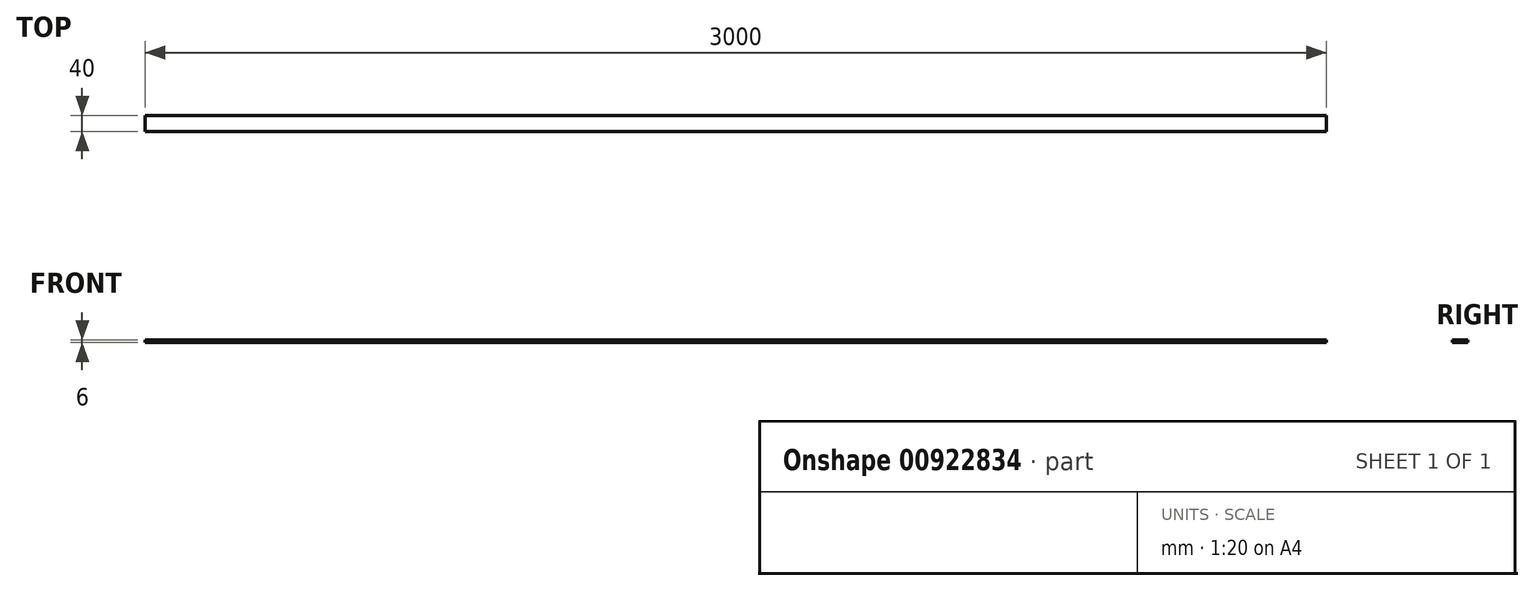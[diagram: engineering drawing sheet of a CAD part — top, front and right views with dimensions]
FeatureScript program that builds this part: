
annotation { "Feature Type Name" : "Feature", "Feature Type Description" : "" }
export const myFeature = defineFeature(function(context is Context, id is Id, definition is map)
    precondition{}
    {
        {
            var Q0;
            Q0=qCreatedBy(makeId("Top.planeOp"),FACE);
            var sketch = newSketch(context, id + "F0", { "sketchPlane" : qUnion([Q0])});
            skLineSegment(sketch, "E0.bottom", {"start": v(1500, 20) * mm, "end": v(-1500, 20) * mm});
            skLineSegment(sketch, "E0.top", {"start": v(1500, -20) * mm, "end": v(-1500, -20) * mm});
            skLineSegment(sketch, "E0.left", {"start": v(1500, 20) * mm, "end": v(1500, -20) * mm});
            skLineSegment(sketch, "E0.right", {"start": v(-1500, 20) * mm, "end": v(-1500, -20) * mm});
            skPoint(sketch, "E0.middle", {"position": v(0, 0) * mm});
            skSolve(sketch);
        }
        {
            var Q0;
            Q0=makeQuery(id+"F0.imprint","IMPRINT",FACE,{"disambiguationData":[TD([[makeQuery(id+"F0.imprint","IMPRINT",EDGE,{"derivedFrom":sQuery(id+"F0.wireOp",EDGE,"E0.bottom")}),1.0]])]});
            extrude(context, id + "F1", {"entities" : qUnion([Q0]), "depth" : 6 * mm, "offsetDistance" : 25 * mm});
        }
    });
